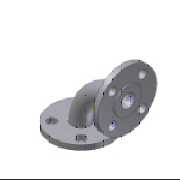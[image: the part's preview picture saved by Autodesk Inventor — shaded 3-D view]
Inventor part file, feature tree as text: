
AUTODESK INVENTOR PART (.ipt)
format: ipt  version: 2023.2 (Build 272271030, 271C)  size: 311,296 bytes
history: native  units: mm (DEFAULTED — no unit token found)
features: sketch x5, other x4, revolve x2, extrude x2, pattern_circular x2, sweep x1
ambient origin geometry x8: Origin, YZ Plane, XZ Plane, XY Plane, X Axis, Y Axis, Z Axis, Center Point
bodies: Solid1 (feature_tree)
feature tree (16):
  sketch  "Sketch1"  dims[d0=387.0mm d1=600.0mm]
  revolve  "Revolution1"  [1 undecoded]
  revolve  "Revolution2"  [1 undecoded]
  sweep  "Sweep1"
  extrude  "Extrusion1"  Depth=37.0mm
  pattern_circular  "Circular Pattern1"  Count=47  [1 undecoded]
  extrude  "Extrusion2"  Depth=600.0mm
  pattern_circular  "Circular Pattern2"  [2 undecoded]
  other  "Work Point1"
  other  "Work Point2"
  other  "Work Axis1"
  other  "Work Axis2"
  sketch  "Sketch2"  dims[d2=470.0mm d3=2.0mm]
  sketch  "Sketch3"  dims[d4=37.0mm d5=90.0deg]
  sketch  "Sketch6"  dims[d6=2.0mm d7=37.0mm]
  sketch  "Sketch7"  dims[d8=387.0mm d9=470.0mm d10=600.0mm d11=381.0mm d12=381.0mm d13=90.0deg d14=409.2mm d15=0.0mm d16=160.0mm d17=360.0deg d18=160.0mm d19=360.0deg d20=1.963495mm d21=29.5mm d22=540.0mm d34=25.4mm d24=0.0mm d25=1.963495mm d26=29.5mm d27=540.0mm d39=25.4mm d28=0.0mm d41=0.0mm]
note: 5 required parameter values undecoded (feature->parameter linkage not recoverable at this tier; creation-order binding heuristic only, values carry confidence <= 0.55)